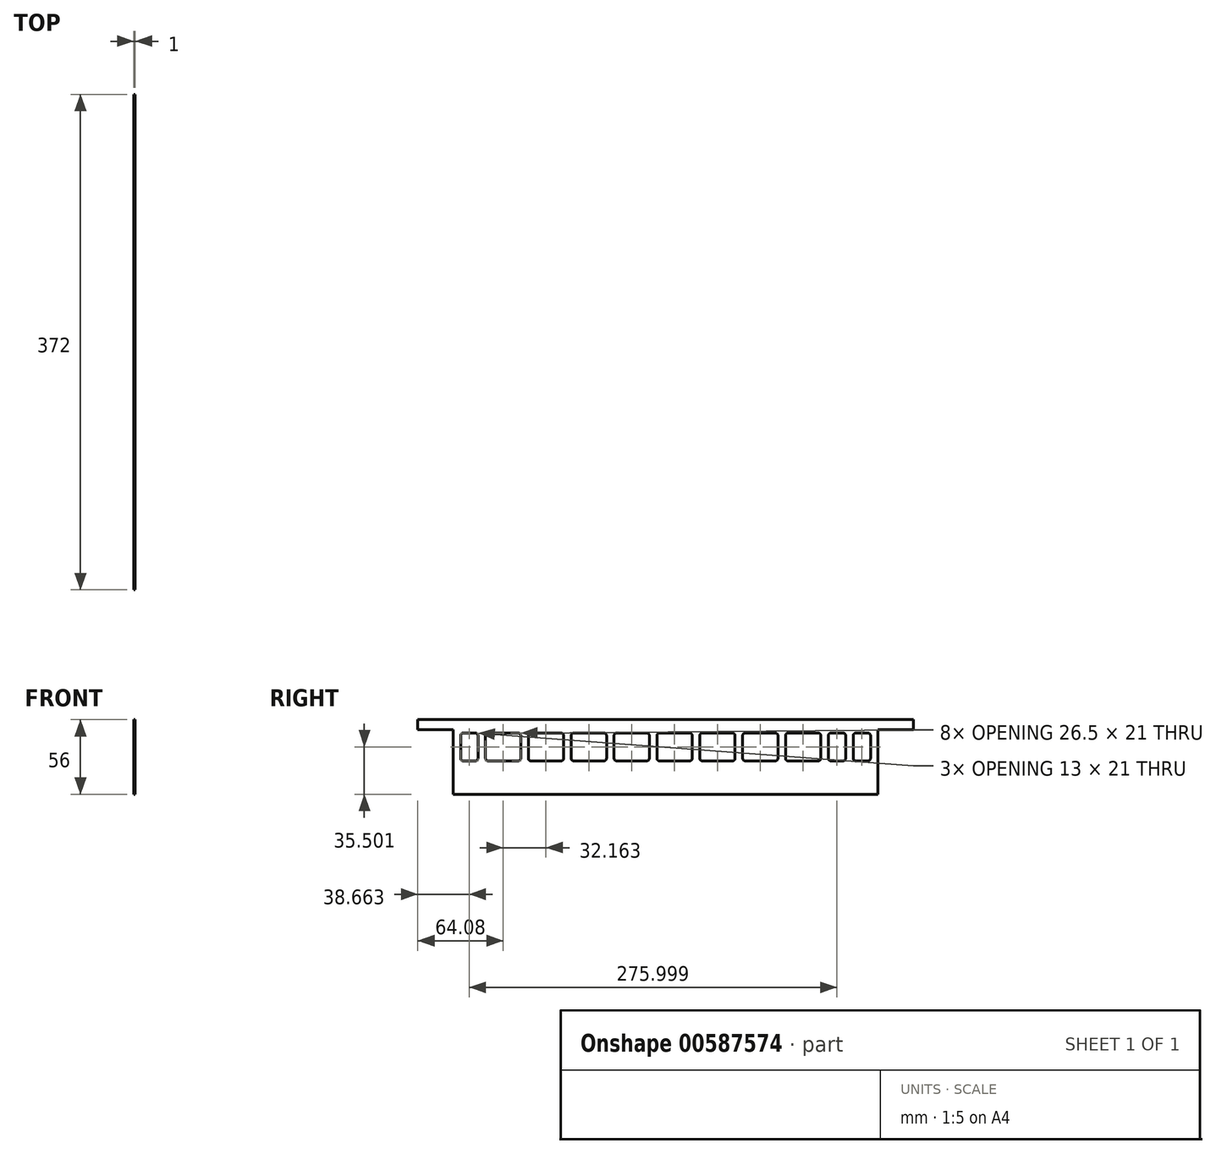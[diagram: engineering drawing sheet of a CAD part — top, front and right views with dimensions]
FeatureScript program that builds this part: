
annotation { "Feature Type Name" : "Feature", "Feature Type Description" : "" }
export const myFeature = defineFeature(function(context is Context, id is Id, definition is map)
    precondition{}
    {
        {
            var Q0;
            Q0=qCreatedBy(makeId("Right.planeOp"),FACE);
            var sketch = newSketch(context, id + "F0", { "sketchPlane" : qUnion([Q0])});
            skLineSegment(sketch, "E0.bottom", {"start": v(-29.83, 39.71) * mm, "end": v(289.17, 39.71) * mm});
            skLineSegment(sketch, "E0.top", {"start": v(-29.83, -16.29) * mm, "end": v(289.17, -16.29) * mm});
            skLineSegment(sketch, "E0.left", {"start": v(-29.83, 32.21) * mm, "end": v(-29.83, -16.29) * mm});
            skLineSegment(sketch, "E0.right", {"start": v(289.17, 32.21) * mm, "end": v(289.17, -16.29) * mm});
            skLineSegment(sketch, "E1.bottom", {"start": v(-29.83, 39.71) * mm, "end": v(-56.33, 39.71) * mm});
            skLineSegment(sketch, "E1.top", {"start": v(-29.83, 32.21) * mm, "end": v(-56.33, 32.21) * mm});
            skLineSegment(sketch, "E1.right", {"start": v(-56.33, 39.71) * mm, "end": v(-56.33, 32.21) * mm});
            skLineSegment(sketch, "E2.bottom", {"start": v(289.17, 39.71) * mm, "end": v(315.67, 39.71) * mm});
            skLineSegment(sketch, "E2.top", {"start": v(289.17, 32.21) * mm, "end": v(315.67, 32.21) * mm});
            skLineSegment(sketch, "E2.right", {"start": v(315.67, 39.71) * mm, "end": v(315.67, 32.21) * mm});
            skLineSegment(sketch, "E3.bottom", {"start": v(-22.17, 29.71) * mm, "end": v(-13.17, 29.71) * mm});
            skLineSegment(sketch, "E3.top", {"start": v(-22.17, 8.71) * mm, "end": v(-13.17, 8.71) * mm});
            skLineSegment(sketch, "E3.left", {"start": v(-24.17, 27.71) * mm, "end": v(-24.17, 10.71) * mm});
            skLineSegment(sketch, "E3.right", {"start": v(-11.17, 27.71) * mm, "end": v(-11.17, 10.71) * mm});
            skLineSegment(sketch, "E4.bottom", {"start": v(-3.5, 29.71) * mm, "end": v(19, 29.71) * mm});
            skLineSegment(sketch, "E4.top", {"start": v(-3.5, 8.71) * mm, "end": v(19, 8.71) * mm});
            skLineSegment(sketch, "E4.left", {"start": v(-5.5, 27.71) * mm, "end": v(-5.5, 10.71) * mm});
            skLineSegment(sketch, "E4.right", {"start": v(21, 27.71) * mm, "end": v(21, 10.71) * mm});
            skPoint(sketch, "E5.visualSharp", {"position": v(-24.17, 29.71) * mm});
            skArc(sketch, "E5.filletArc", {"start": v(-22.17, 29.71) * mm, "mid": v(-23.58, 29.12) * mm, "end": v(-24.17, 27.71) * mm});
            skPoint(sketch, "E6.visualSharp", {"position": v(-11.17, 29.71) * mm});
            skArc(sketch, "E6.filletArc", {"start": v(-11.17, 27.71) * mm, "mid": v(-11.75, 29.12) * mm, "end": v(-13.17, 29.71) * mm});
            skPoint(sketch, "E7.visualSharp", {"position": v(-24.17, 8.71) * mm});
            skArc(sketch, "E7.filletArc", {"start": v(-24.17, 10.71) * mm, "mid": v(-23.58, 9.3) * mm, "end": v(-22.17, 8.71) * mm});
            skPoint(sketch, "E8.visualSharp", {"position": v(-11.17, 8.71) * mm});
            skArc(sketch, "E8.filletArc", {"start": v(-13.17, 8.71) * mm, "mid": v(-11.75, 9.3) * mm, "end": v(-11.17, 10.71) * mm});
            skPoint(sketch, "E9.visualSharp", {"position": v(-5.5, 8.71) * mm});
            skArc(sketch, "E9.filletArc", {"start": v(-5.5, 10.71) * mm, "mid": v(-4.91, 9.3) * mm, "end": v(-3.5, 8.71) * mm});
            skPoint(sketch, "E10.visualSharp", {"position": v(-5.5, 29.71) * mm});
            skArc(sketch, "E10.filletArc", {"start": v(-3.5, 29.71) * mm, "mid": v(-4.91, 29.12) * mm, "end": v(-5.5, 27.71) * mm});
            skPoint(sketch, "E11.visualSharp", {"position": v(21, 29.71) * mm});
            skArc(sketch, "E11.filletArc", {"start": v(21, 27.71) * mm, "mid": v(20.41, 29.12) * mm, "end": v(19, 29.71) * mm});
            skPoint(sketch, "E12.visualSharp", {"position": v(21, 8.71) * mm});
            skArc(sketch, "E12.filletArc", {"start": v(19, 8.71) * mm, "mid": v(20.41, 9.3) * mm, "end": v(21, 10.71) * mm});
            skLineSegment(sketch, "E13.bottom", {"start": v(28.66, 29.71) * mm, "end": v(51.16, 29.71) * mm});
            skLineSegment(sketch, "E13.top", {"start": v(28.66, 8.71) * mm, "end": v(51.16, 8.71) * mm});
            skLineSegment(sketch, "E13.left", {"start": v(26.66, 27.71) * mm, "end": v(26.66, 10.71) * mm});
            skLineSegment(sketch, "E13.right", {"start": v(53.16, 27.71) * mm, "end": v(53.16, 10.71) * mm});
            skLineSegment(sketch, "E14.bottom", {"start": v(60.83, 29.71) * mm, "end": v(83.33, 29.71) * mm});
            skLineSegment(sketch, "E14.top", {"start": v(60.83, 8.71) * mm, "end": v(83.33, 8.71) * mm});
            skLineSegment(sketch, "E14.left", {"start": v(58.83, 27.71) * mm, "end": v(58.83, 10.71) * mm});
            skLineSegment(sketch, "E14.right", {"start": v(85.33, 27.71) * mm, "end": v(85.33, 10.71) * mm});
            skLineSegment(sketch, "E15.bottom", {"start": v(93, 29.71) * mm, "end": v(115.5, 29.71) * mm});
            skLineSegment(sketch, "E15.top", {"start": v(93, 8.71) * mm, "end": v(115.5, 8.71) * mm});
            skLineSegment(sketch, "E15.left", {"start": v(91, 27.71) * mm, "end": v(91, 10.71) * mm});
            skLineSegment(sketch, "E15.right", {"start": v(117.5, 27.71) * mm, "end": v(117.5, 10.71) * mm});
            skLineSegment(sketch, "E16.bottom", {"start": v(125.16, 29.71) * mm, "end": v(147.66, 29.71) * mm});
            skLineSegment(sketch, "E16.top", {"start": v(125.16, 8.71) * mm, "end": v(147.66, 8.71) * mm});
            skLineSegment(sketch, "E16.left", {"start": v(123.16, 27.71) * mm, "end": v(123.16, 10.71) * mm});
            skLineSegment(sketch, "E16.right", {"start": v(149.66, 27.71) * mm, "end": v(149.66, 10.71) * mm});
            skPoint(sketch, "E17.oppositeSnap0", {"position": v(72.08, 8.71) * mm});
            skLineSegment(sketch, "E17.bottom", {"start": v(157.33, 29.71) * mm, "end": v(179.83, 29.71) * mm});
            skLineSegment(sketch, "E17.top", {"start": v(157.33, 8.71) * mm, "end": v(179.83, 8.71) * mm});
            skLineSegment(sketch, "E17.left", {"start": v(155.33, 27.71) * mm, "end": v(155.33, 10.71) * mm});
            skLineSegment(sketch, "E17.right", {"start": v(181.83, 27.71) * mm, "end": v(181.83, 10.71) * mm});
            skLineSegment(sketch, "E18.bottom", {"start": v(189.5, 29.71) * mm, "end": v(212, 29.71) * mm});
            skLineSegment(sketch, "E18.top", {"start": v(189.5, 8.71) * mm, "end": v(212, 8.71) * mm});
            skLineSegment(sketch, "E18.left", {"start": v(187.5, 27.71) * mm, "end": v(187.5, 10.71) * mm});
            skLineSegment(sketch, "E18.right", {"start": v(214, 27.71) * mm, "end": v(214, 10.71) * mm});
            skLineSegment(sketch, "E19.bottom", {"start": v(221.66, 29.71) * mm, "end": v(244.17, 29.71) * mm});
            skLineSegment(sketch, "E19.top", {"start": v(221.66, 8.71) * mm, "end": v(244.17, 8.71) * mm});
            skLineSegment(sketch, "E19.left", {"start": v(219.66, 27.71) * mm, "end": v(219.66, 10.71) * mm});
            skLineSegment(sketch, "E19.right", {"start": v(246.16, 27.71) * mm, "end": v(246.16, 10.71) * mm});
            skLineSegment(sketch, "E20.bottom", {"start": v(253.83, 29.71) * mm, "end": v(262.83, 29.71) * mm});
            skLineSegment(sketch, "E20.top", {"start": v(253.83, 8.71) * mm, "end": v(262.83, 8.71) * mm});
            skLineSegment(sketch, "E20.left", {"start": v(251.83, 27.71) * mm, "end": v(251.83, 10.71) * mm});
            skLineSegment(sketch, "E20.right", {"start": v(264.83, 27.71) * mm, "end": v(264.83, 10.71) * mm});
            skLineSegment(sketch, "E21.bottom", {"start": v(272.5, 29.71) * mm, "end": v(281.5, 29.71) * mm});
            skLineSegment(sketch, "E21.top", {"start": v(272.5, 8.71) * mm, "end": v(281.5, 8.71) * mm});
            skLineSegment(sketch, "E21.left", {"start": v(270.5, 27.71) * mm, "end": v(270.5, 10.71) * mm});
            skLineSegment(sketch, "E21.right", {"start": v(283.5, 27.71) * mm, "end": v(283.5, 10.71) * mm});
            skPoint(sketch, "E22.visualSharp", {"position": v(26.66, 29.71) * mm});
            skArc(sketch, "E22.filletArc", {"start": v(28.66, 29.71) * mm, "mid": v(27.25, 29.12) * mm, "end": v(26.66, 27.71) * mm});
            skPoint(sketch, "E23.visualSharp", {"position": v(53.16, 29.71) * mm});
            skArc(sketch, "E23.filletArc", {"start": v(53.16, 27.71) * mm, "mid": v(52.58, 29.12) * mm, "end": v(51.16, 29.71) * mm});
            skPoint(sketch, "E24.visualSharp", {"position": v(58.83, 29.71) * mm});
            skArc(sketch, "E24.filletArc", {"start": v(60.83, 29.71) * mm, "mid": v(59.42, 29.12) * mm, "end": v(58.83, 27.71) * mm});
            skPoint(sketch, "E25.visualSharp", {"position": v(85.33, 29.71) * mm});
            skArc(sketch, "E25.filletArc", {"start": v(85.33, 27.71) * mm, "mid": v(84.74, 29.12) * mm, "end": v(83.33, 29.71) * mm});
            skPoint(sketch, "E26.visualSharp", {"position": v(91, 29.71) * mm});
            skArc(sketch, "E26.filletArc", {"start": v(93, 29.71) * mm, "mid": v(91.58, 29.12) * mm, "end": v(91, 27.71) * mm});
            skPoint(sketch, "E27.visualSharp", {"position": v(117.5, 29.71) * mm});
            skArc(sketch, "E27.filletArc", {"start": v(117.5, 27.71) * mm, "mid": v(116.91, 29.12) * mm, "end": v(115.5, 29.71) * mm});
            skPoint(sketch, "E28.visualSharp", {"position": v(123.16, 29.71) * mm});
            skArc(sketch, "E28.filletArc", {"start": v(125.16, 29.71) * mm, "mid": v(123.75, 29.12) * mm, "end": v(123.16, 27.71) * mm});
            skPoint(sketch, "E29.visualSharp", {"position": v(149.66, 29.71) * mm});
            skArc(sketch, "E29.filletArc", {"start": v(149.66, 27.71) * mm, "mid": v(149.08, 29.12) * mm, "end": v(147.66, 29.71) * mm});
            skPoint(sketch, "E30.visualSharp", {"position": v(155.33, 29.71) * mm});
            skArc(sketch, "E30.filletArc", {"start": v(157.33, 29.71) * mm, "mid": v(155.92, 29.12) * mm, "end": v(155.33, 27.71) * mm});
            skPoint(sketch, "E31.visualSharp", {"position": v(181.83, 29.71) * mm});
            skArc(sketch, "E31.filletArc", {"start": v(181.83, 27.71) * mm, "mid": v(181.25, 29.12) * mm, "end": v(179.83, 29.71) * mm});
            skPoint(sketch, "E32.visualSharp", {"position": v(187.5, 29.71) * mm});
            skArc(sketch, "E32.filletArc", {"start": v(189.5, 29.71) * mm, "mid": v(188.08, 29.12) * mm, "end": v(187.5, 27.71) * mm});
            skPoint(sketch, "E33.visualSharp", {"position": v(214, 29.71) * mm});
            skArc(sketch, "E33.filletArc", {"start": v(214, 27.71) * mm, "mid": v(213.41, 29.12) * mm, "end": v(212, 29.71) * mm});
            skPoint(sketch, "E34.visualSharp", {"position": v(219.66, 29.71) * mm});
            skArc(sketch, "E34.filletArc", {"start": v(221.66, 29.71) * mm, "mid": v(220.25, 29.12) * mm, "end": v(219.66, 27.71) * mm});
            skPoint(sketch, "E35.visualSharp", {"position": v(246.16, 29.71) * mm});
            skArc(sketch, "E35.filletArc", {"start": v(246.17, 27.71) * mm, "mid": v(245.58, 29.12) * mm, "end": v(244.17, 29.71) * mm});
            skPoint(sketch, "E36.visualSharp", {"position": v(251.83, 29.71) * mm});
            skArc(sketch, "E36.filletArc", {"start": v(253.83, 29.71) * mm, "mid": v(252.42, 29.12) * mm, "end": v(251.83, 27.71) * mm});
            skPoint(sketch, "E37.visualSharp", {"position": v(264.83, 29.71) * mm});
            skArc(sketch, "E37.filletArc", {"start": v(264.83, 27.71) * mm, "mid": v(264.25, 29.12) * mm, "end": v(262.83, 29.71) * mm});
            skPoint(sketch, "E38.visualSharp", {"position": v(270.5, 29.71) * mm});
            skArc(sketch, "E38.filletArc", {"start": v(272.5, 29.71) * mm, "mid": v(271.08, 29.12) * mm, "end": v(270.5, 27.71) * mm});
            skPoint(sketch, "E39.visualSharp", {"position": v(283.5, 29.71) * mm});
            skArc(sketch, "E39.filletArc", {"start": v(283.5, 27.71) * mm, "mid": v(282.91, 29.12) * mm, "end": v(281.5, 29.71) * mm});
            skPoint(sketch, "E40.visualSharp", {"position": v(283.5, 8.71) * mm});
            skArc(sketch, "E40.filletArc", {"start": v(281.5, 8.71) * mm, "mid": v(282.91, 9.3) * mm, "end": v(283.5, 10.71) * mm});
            skPoint(sketch, "E41.visualSharp", {"position": v(270.5, 8.71) * mm});
            skArc(sketch, "E41.filletArc", {"start": v(270.5, 10.71) * mm, "mid": v(271.08, 9.3) * mm, "end": v(272.5, 8.71) * mm});
            skPoint(sketch, "E42.visualSharp", {"position": v(264.83, 8.71) * mm});
            skArc(sketch, "E42.filletArc", {"start": v(262.83, 8.71) * mm, "mid": v(264.25, 9.3) * mm, "end": v(264.83, 10.71) * mm});
            skPoint(sketch, "E43.visualSharp", {"position": v(251.83, 8.71) * mm});
            skArc(sketch, "E43.filletArc", {"start": v(251.83, 10.71) * mm, "mid": v(252.42, 9.3) * mm, "end": v(253.83, 8.71) * mm});
            skPoint(sketch, "E44.visualSharp", {"position": v(246.16, 8.71) * mm});
            skArc(sketch, "E44.filletArc", {"start": v(244.17, 8.71) * mm, "mid": v(245.58, 9.3) * mm, "end": v(246.17, 10.71) * mm});
            skPoint(sketch, "E45.visualSharp", {"position": v(219.66, 8.71) * mm});
            skArc(sketch, "E45.filletArc", {"start": v(219.66, 10.71) * mm, "mid": v(220.25, 9.3) * mm, "end": v(221.66, 8.71) * mm});
            skPoint(sketch, "E46.visualSharp", {"position": v(214, 8.71) * mm});
            skArc(sketch, "E46.filletArc", {"start": v(212, 8.71) * mm, "mid": v(213.41, 9.3) * mm, "end": v(214, 10.71) * mm});
            skPoint(sketch, "E47.visualSharp", {"position": v(187.5, 8.71) * mm});
            skArc(sketch, "E47.filletArc", {"start": v(187.5, 10.71) * mm, "mid": v(188.08, 9.3) * mm, "end": v(189.5, 8.71) * mm});
            skPoint(sketch, "E48.visualSharp", {"position": v(181.83, 8.71) * mm});
            skArc(sketch, "E48.filletArc", {"start": v(179.83, 8.71) * mm, "mid": v(181.25, 9.3) * mm, "end": v(181.83, 10.71) * mm});
            skPoint(sketch, "E49.visualSharp", {"position": v(155.33, 8.71) * mm});
            skArc(sketch, "E49.filletArc", {"start": v(155.33, 10.71) * mm, "mid": v(155.92, 9.3) * mm, "end": v(157.33, 8.71) * mm});
            skPoint(sketch, "E50.visualSharp", {"position": v(149.66, 8.71) * mm});
            skArc(sketch, "E50.filletArc", {"start": v(147.66, 8.71) * mm, "mid": v(149.08, 9.3) * mm, "end": v(149.66, 10.71) * mm});
            skPoint(sketch, "E51.visualSharp", {"position": v(123.16, 8.71) * mm});
            skArc(sketch, "E51.filletArc", {"start": v(123.16, 10.71) * mm, "mid": v(123.75, 9.3) * mm, "end": v(125.16, 8.71) * mm});
            skPoint(sketch, "E52.visualSharp", {"position": v(117.5, 8.71) * mm});
            skArc(sketch, "E52.filletArc", {"start": v(115.5, 8.71) * mm, "mid": v(116.91, 9.3) * mm, "end": v(117.5, 10.71) * mm});
            skPoint(sketch, "E53.visualSharp", {"position": v(91, 8.71) * mm});
            skArc(sketch, "E53.filletArc", {"start": v(91, 10.71) * mm, "mid": v(91.58, 9.3) * mm, "end": v(93, 8.71) * mm});
            skPoint(sketch, "E54.visualSharp", {"position": v(85.33, 8.71) * mm});
            skArc(sketch, "E54.filletArc", {"start": v(83.33, 8.71) * mm, "mid": v(84.74, 9.3) * mm, "end": v(85.33, 10.71) * mm});
            skPoint(sketch, "E55.visualSharp", {"position": v(58.83, 8.71) * mm});
            skArc(sketch, "E55.filletArc", {"start": v(58.83, 10.71) * mm, "mid": v(59.42, 9.3) * mm, "end": v(60.83, 8.71) * mm});
            skPoint(sketch, "E56.visualSharp", {"position": v(53.16, 8.71) * mm});
            skArc(sketch, "E56.filletArc", {"start": v(51.16, 8.71) * mm, "mid": v(52.58, 9.3) * mm, "end": v(53.16, 10.71) * mm});
            skPoint(sketch, "E57.visualSharp", {"position": v(26.66, 8.71) * mm});
            skArc(sketch, "E57.filletArc", {"start": v(26.66, 10.71) * mm, "mid": v(27.25, 9.3) * mm, "end": v(28.66, 8.71) * mm});
            skSolve(sketch);
        }
        {
            var Q0;
            Q0=makeQuery(id+"F0.imprint","IMPRINT",FACE,{"disambiguationData":[TD([[makeQuery(id+"F0.imprint","IMPRINT",EDGE,{"derivedFrom":sQuery(id+"F0.wireOp",EDGE,"E0.bottom")}),-1.0]])]});
            extrude(context, id + "F1", {"entities" : qUnion([Q0]), "depth" : 1 * mm, "offsetDistance" : 25 * mm});
        }
    });
